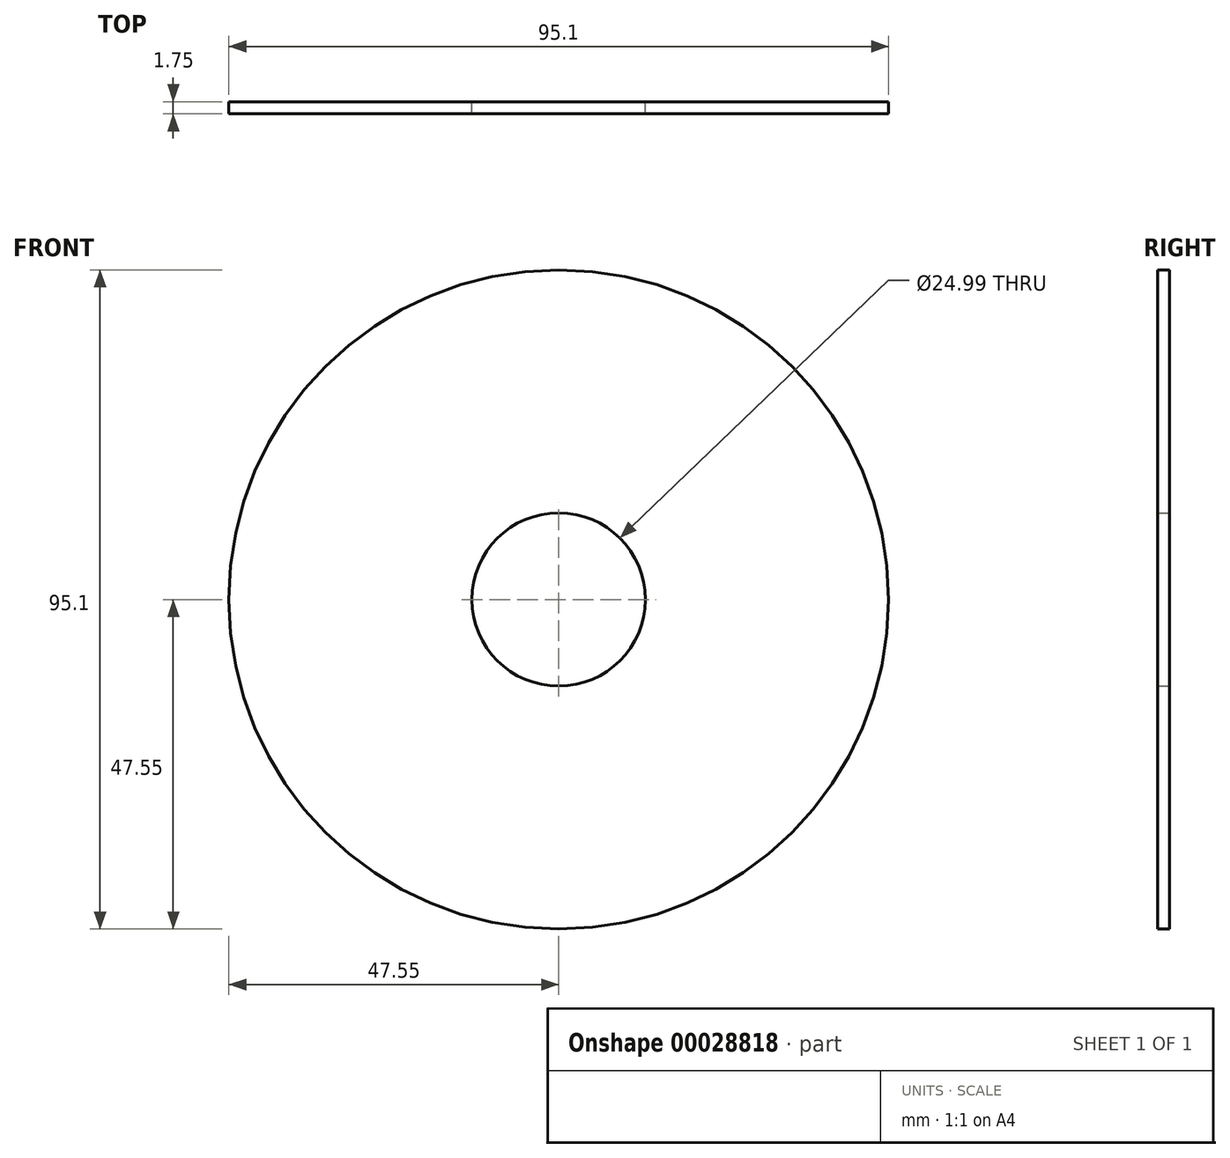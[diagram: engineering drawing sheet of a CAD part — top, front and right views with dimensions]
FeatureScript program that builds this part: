
annotation { "Feature Type Name" : "Feature", "Feature Type Description" : "" }
export const myFeature = defineFeature(function(context is Context, id is Id, definition is map)
    precondition{}
    {
        {
            var Q0;
            Q0=qCreatedBy(makeId("Front.planeOp"),FACE);
            var sketch = newSketch(context, id + "F0", { "sketchPlane" : qUnion([Q0])});
            skCircle(sketch, "E0", {"center": v(0, 0) * mm, "radius": 47.55 * mm});
            skCircle(sketch, "E1", {"center": v(0, 0) * mm, "radius": 12.5 * mm});
            skSolve(sketch);
        }
        {
            var Q0;
            Q0 = qSketchRegion(id + "F0", true);
            extrude(context, id + "F1", {"entities" : qUnion([Q0]), "depth" : 1.75 * mm});
        }
    });
